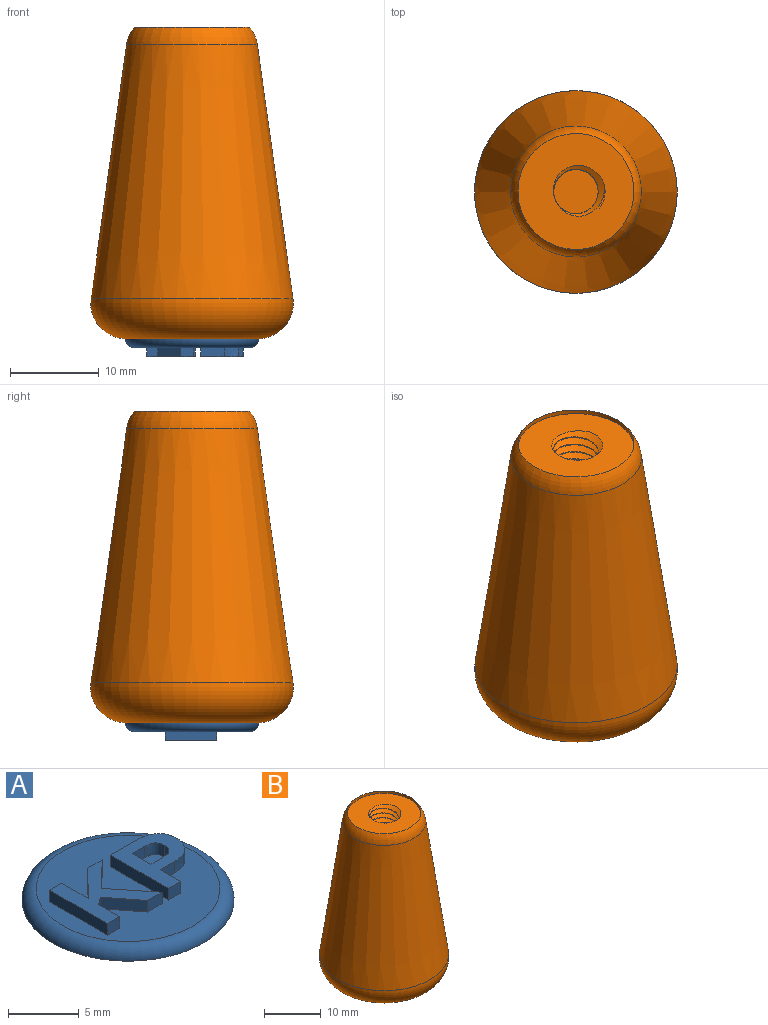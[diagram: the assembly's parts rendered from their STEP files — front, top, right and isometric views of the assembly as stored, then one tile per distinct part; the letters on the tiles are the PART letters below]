
ASSEMBLY  parts=2 mates=1
PART A: 34 faces, bbox 16.2x16.2x2 mm
  f0: plane 13x13mm, normal (0,0,1), area 98.2mm2, adj f2,f3,f4,f5,f6,f7,f8,f9
  f1: plane 15x15mm, normal (0,0,-1), area 176.7mm2, adj f33
  f2: plane 2.66x2.08mm, normal (-0.79,-0.62,0), area 3.4mm2, adj f0,f3,f13,f14
  f3: plane 1.43x1mm, normal (0,-1,0), area 1.4mm2, adj f0,f2,f4,f14
  f4: plane 3.35x2.68mm, normal (0.78,0.63,0), area 4.3mm2, adj f0,f3,f5,f14
  f5: plane 2.48x2.45mm, normal (0.7,-0.71,0), area 3.5mm2, adj f0,f4,f6,f14
  f6: plane 1.42x1mm, normal (0,1,0), area 1.4mm2, adj f0,f5,f7,f14
  f7: plane 2.63x2.61mm, normal (-0.71,0.7,0), area 3.7mm2, adj f0,f6,f8,f14
  f8: plane 2.63x1mm, normal (1,0,0), area 2.6mm2, adj f0,f7,f9,f14
  f9: plane 1.21x1mm, normal (0,1,0), area 1.2mm2, adj f0,f8,f10,f14
  f10: plane 5.8x1mm, normal (-1,0,0), area 5.8mm2, adj f0,f9,f11,f14
  f11: plane 1.21x1mm, normal (0,-1,0), area 1.2mm2, adj f0,f10,f12,f14
  f12: plane 2.11x1mm, normal (1,0,0), area 2.1mm2, adj f0,f11,f13,f14
  f13: plane 1x0.72mm, normal (0.61,-0.79,0), area 0.9mm2, adj f0,f2,f12,f14
  f14: plane 5.8x5.44mm, normal (0,0,1), area 15.6mm2, adj f2,f3,f4,f5,f6,f7,f8,f9
  f15: extruded ~1.08x1mm, area 1.6mm2, adj f16,f30,f31,f32
  f16: extruded ~1x0.72mm, area 0.8mm2, adj f15,f17,f31,f32
  f17: extruded ~1x0.77mm, area 0.8mm2, adj f16,f18,f31,f32
  f18: plane 1.29x1mm, normal (0,1,0), area 1.3mm2, adj f17,f19,f31,f32
  f19: plane 1.88x1mm, normal (1,0,0), area 1.9mm2, adj f18,f30,f31,f32
  f20: extruded ~1x1mm, area 1mm2, adj f0,f21,f29,f31
  f21: extruded ~1.36x1mm, area 1.5mm2, adj f0,f20,f22,f31
  f22: extruded ~1.6x1mm, area 1.7mm2, adj f0,f21,f23,f31
  f23: plane 2.6x1mm, normal (0,1,0), area 2.6mm2, adj f0,f22,f24,f31
  f24: plane 5.8x1mm, normal (-1,0,0), area 5.8mm2, adj f0,f23,f25,f31
  f25: plane 1.21x1mm, normal (0,-1,0), area 1.2mm2, adj f0,f24,f26,f31
  f26: plane 2.04x1mm, normal (1,0,0), area 2mm2, adj f0,f25,f27,f31
  f27: plane 1.44x1mm, normal (0,-1,0), area 1.4mm2, adj f0,f26,f28,f31
  f28: extruded ~1.13x1mm, area 1.2mm2, adj f0,f27,f29,f31
  f29: extruded ~1x0.73mm, area 1mm2, adj f0,f20,f28,f31
  f30: plane 1.25x1mm, normal (0,-1,0), area 1.3mm2, adj f15,f19,f31,f32
  f31: plane 5.8x4.77mm, normal (0,0,1), area 14.9mm2, adj f15,f16,f17,f18,f19,f20,f21,f22
  f32: plane 2.33x1.88mm, normal (0,0,1), area 4mm2, adj f15,f16,f17,f18,f19,f30
  f33: torus R=6.5mm, axis (0,0,1), area 70.4mm2, adj f0,f1
PART B: 11 faces, bbox 25.3x25.3x35.7 mm
  f0: cylinder r=2.5mm len=14.5mm, axis (0,0,1), area -1.4mm2, adj f5,f6,f7,f8,f9
  f1: cone r=12mm half-angle=8deg, axis (0,0,-1), area 1691.9mm2, adj f3,f10
  f2: plane 14.8x14.8mm, normal (0,0,-1), area 172mm2, adj f3
  f3: torus R=7.4mm, axis (0,0,1), area 432.6mm2, adj f1,f2
  f4: cylinder r=6.51mm len=13.03mm, axis (0,0,1), area 20.5mm2, adj f5,f10
  f5: plane 13.61x13.61mm, normal (0,0,1), area 107.6mm2, adj f0,f4,f8,f9
  f6: plane 5x5mm, normal (0,0,1), area 19.6mm2, adj f0
  f7: plane 0.9x0.78mm, normal (0,1,0), area 0.4mm2, adj f0,f8,f9
  f8: bspline ~14.95x7.57mm, area 233.8mm2, adj f0,f5,f7,f9
  f9: bspline ~14.78x7.57mm, area 225.8mm2, adj f0,f5,f7,f8
  f10: torus R=3.39mm, axis (0,0,1), area 94.6mm2, adj f1,f4
PLACE A rot(axis=(1,0,0),180deg) t=(0.2,-0.35,-23.77)mm
PLACE B t=(0.2,-0.35,-23.77)mm
MATE fastened B.f1 <-> A.f33  axis (0,0,-1) through (0.2,-0.35,-23.77)mm
